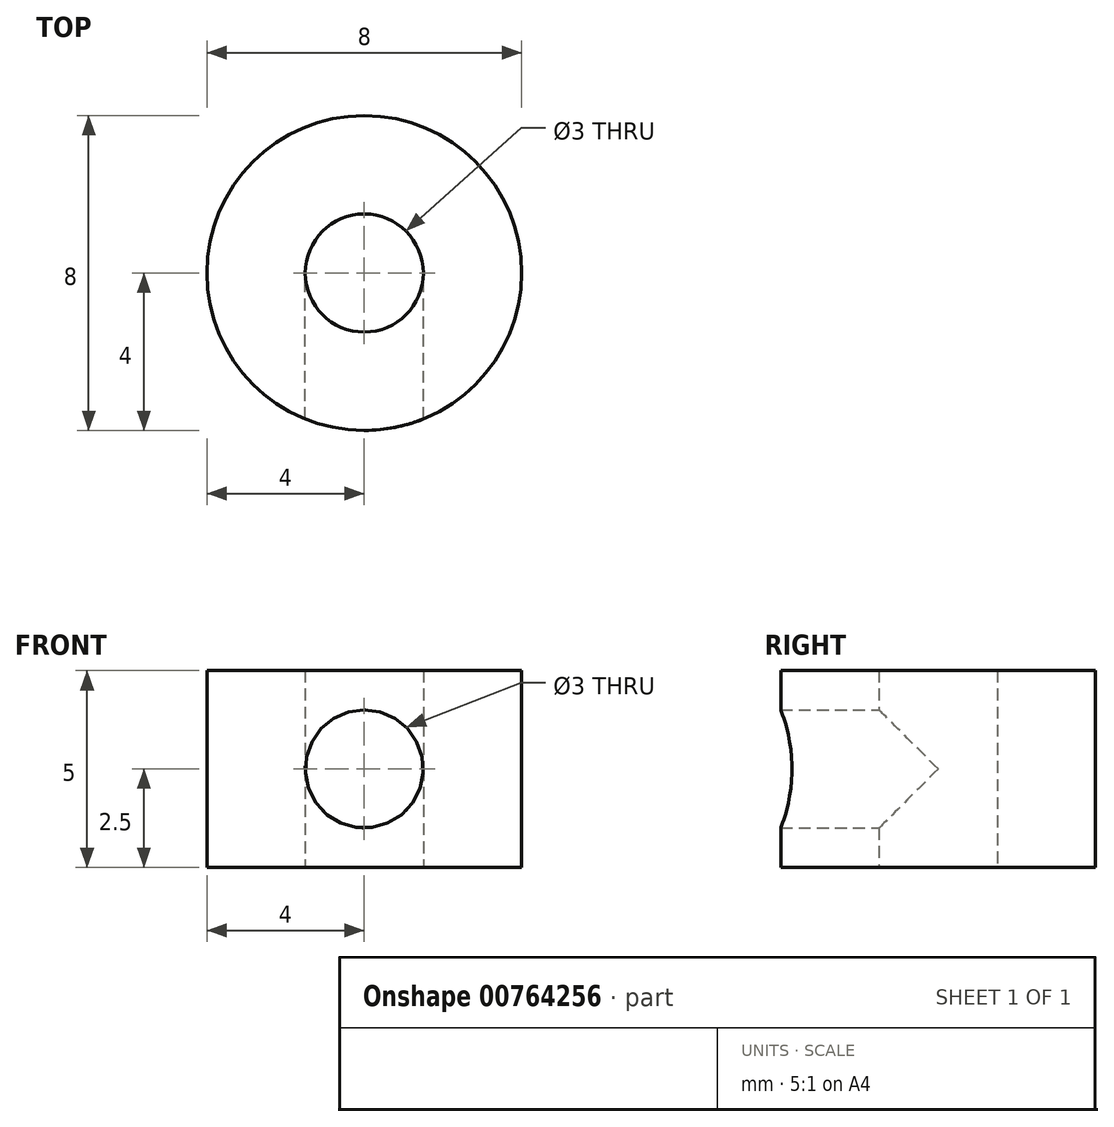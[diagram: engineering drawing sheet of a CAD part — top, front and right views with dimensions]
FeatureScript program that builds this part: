
annotation { "Feature Type Name" : "Feature", "Feature Type Description" : "" }
export const myFeature = defineFeature(function(context is Context, id is Id, definition is map)
    precondition{}
    {
        {
            var Q0;
            Q0=qCreatedBy(makeId("Top.planeOp"),FACE);
            var sketch = newSketch(context, id + "F0", { "sketchPlane" : qUnion([Q0])});
            skCircle(sketch, "E0", {"center": v(0, 0) * mm, "radius": 4 * mm});
            skCircle(sketch, "E1", {"center": v(0, 0) * mm, "radius": 1.5 * mm});
            skSolve(sketch);
        }
        {
            var Q0;
            Q0 = qSketchRegion(id + "F0", true);
            extrude(context, id + "F1", {"entities" : qUnion([Q0]), "depth" : 5 * mm, "offsetDistance" : 25 * mm});
        }
        {
            var Q0;
            Q0=qCreatedBy(makeId("Front.planeOp"),FACE);
            var sketch = newSketch(context, id + "F2", { "sketchPlane" : qUnion([Q0])});
            skCircle(sketch, "E2", {"center": v(0, 2.5) * mm, "radius": 1.5 * mm});
            skSolve(sketch);
        }
        {
            var Q0;
            Q0 = qSketchRegion(id + "F2", true);
            extrude(context, id + "F3", {"entities" : qUnion([Q0]), "operationType" : NewBodyOperationType.REMOVE, "depth" : 25 * mm, "offsetDistance" : 25 * mm});
        }
    });
